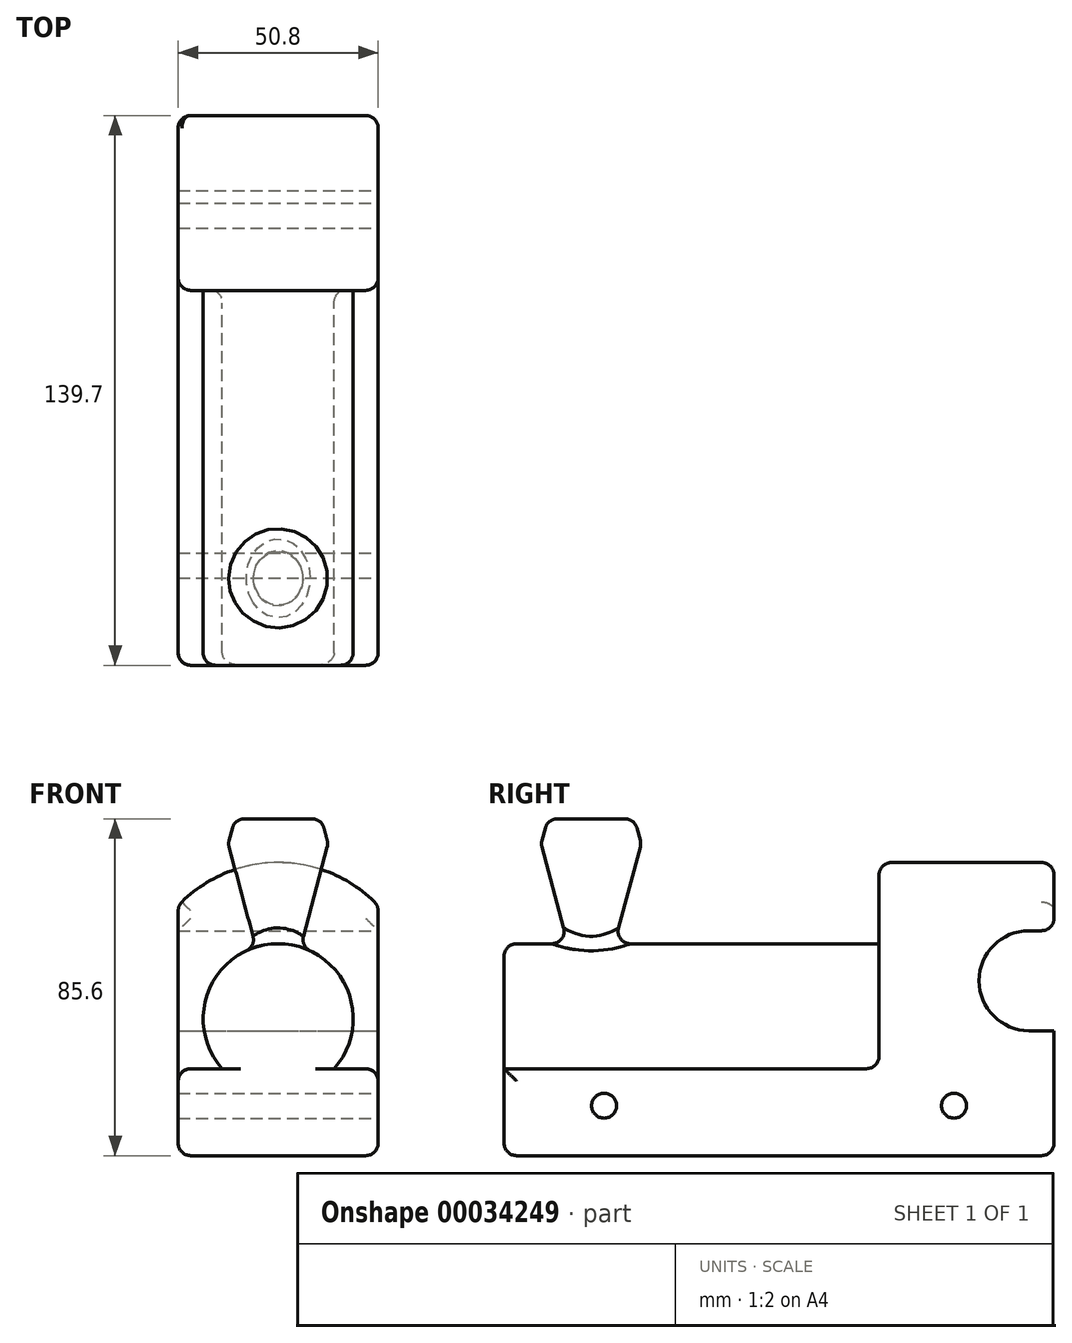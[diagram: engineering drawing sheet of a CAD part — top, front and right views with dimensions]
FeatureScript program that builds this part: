
annotation { "Feature Type Name" : "Feature", "Feature Type Description" : "" }
export const myFeature = defineFeature(function(context is Context, id is Id, definition is map)
    precondition{}
    {
        {
            var Q0;
            Q0=qCreatedBy(makeId("Front.planeOp"),FACE);
            var sketch = newSketch(context, id + "F0", { "sketchPlane" : qUnion([Q0])});
            skLineSegment(sketch, "E0.bottom", {"start": v(-39.2, 59.95) * mm, "end": v(11.6, 59.95) * mm});
            skLineSegment(sketch, "E0.top", {"start": v(-39.2, -3.55) * mm, "end": v(11.6, -3.55) * mm});
            skLineSegment(sketch, "E0.left", {"start": v(-39.2, 59.95) * mm, "end": v(-39.2, -3.55) * mm});
            skLineSegment(sketch, "E0.right", {"start": v(11.6, 59.95) * mm, "end": v(11.6, -3.55) * mm});
            skArc(sketch, "E1", {"start": v(11.6, 59.95) * mm, "mid": v(-13.8, 70.92) * mm, "end": v(-39.2, 59.95) * mm});
            skSolve(sketch);
        }
        {
            var Q0;
            Q0=makeQuery(id+"F0.imprint","IMPRINT",FACE,{"disambiguationData":[TD([[makeQuery(id+"F0.imprint","IMPRINT",EDGE,{"derivedFrom":sQuery(id+"F0.wireOp",EDGE,"E0.bottom")}),1.0]])]});
            var Q1;
            Q1=makeQuery(id+"F0.imprint","IMPRINT",FACE,{"disambiguationData":[TD([[makeQuery(id+"F0.imprint","IMPRINT",EDGE,{"derivedFrom":sQuery(id+"F0.wireOp",EDGE,"E0.bottom")}),-1.0]])]});
            extrude(context, id + "F1", {"entities" : qUnion([Q0, Q1]), "depth" : 139.7 * mm});
        }
        {
            var Q0;
            Q0=makeQuery(id+"F1.opExtrude","CAP_FACE",FACE,{"disambiguationData":[OSD([sQuery(id+"F0.wireOp",EDGE,"E0.top"),sQuery(id+"F0.wireOp",EDGE,"E0.left"),sQuery(id+"F0.wireOp",EDGE,"E0.right"),sQuery(id+"F0.wireOp",EDGE,"E1")])],"isStart":false});
            var sketch = newSketch(context, id + "F2", { "sketchPlane" : qUnion([Q0])});
            skLineSegment(sketch, "E2.bottom", {"start": v(-76.26, 116.12) * mm, "end": v(58.58, 116.12) * mm});
            skLineSegment(sketch, "E2.top", {"start": v(-76.26, 18.55) * mm, "end": v(58.58, 18.55) * mm});
            skLineSegment(sketch, "E2.left", {"start": v(-76.26, 116.12) * mm, "end": v(-76.26, 18.55) * mm});
            skLineSegment(sketch, "E2.right", {"start": v(58.58, 116.12) * mm, "end": v(58.58, 18.55) * mm});
            skSolve(sketch);
        }
        {
            var Q0;
            Q0=makeQuery(id+"F2.imprint","IMPRINT",FACE,{"disambiguationData":[TD([[makeQuery(id+"F2.imprint","IMPRINT",EDGE,{"derivedFrom":sQuery(id+"F2.wireOp",EDGE,"E2.bottom")}),-1.0]])]});
            var Q1;
            {var subQ3=makeQuery(id+"F1.opExtrude","CAP_EDGE",EDGE,{"disambiguationData":[OSD([sQuery(id+"F0.wireOp",EDGE,"E1")])],"isStart":false});Q1=makeQuery(id+"F2.imprint","IMPRINT",FACE,{"disambiguationData":[TD([[makeQuery(id+"F2.imprint","IMPRINT",EDGE,{"derivedFrom":subQ3}),1.0]])]});}
            extrude(context, id + "F3", {"entities" : qUnion([Q0, Q1]), "operationType" : NewBodyOperationType.REMOVE, "oppositeDirection" : true, "depth" : 95.25 * mm});
        }
        {
            var Q0;
            Q0=makeQuery(id+"F3.boolean.opBoolean","COPY",FACE,{"derivedFrom":makeQuery(id+"F3.opExtrude","CAP_FACE",FACE,{"disambiguationData":[OSD([sQuery(id+"F2.wireOp",EDGE,"E2.bottom"),sQuery(id+"F2.wireOp",EDGE,"E2.top"),sQuery(id+"F2.wireOp",EDGE,"E2.left"),sQuery(id+"F2.wireOp",EDGE,"E2.right")])],"isStart":false})});
            var sketch = newSketch(context, id + "F4", { "sketchPlane" : qUnion([Q0])});
            skCircle(sketch, "E3", {"center": v(-13.8, 31.25) * mm, "radius": 19.05 * mm});
            skPoint(sketch, "E4", {"position": v(-13.8, 50.3) * mm});
            skSolve(sketch);
        }
        {
            var Q0;
            {var subQ0=makeQuery(id+"F3.boolean.opBoolean","COPY",EDGE,{"derivedFrom":makeQuery(id+"F3.opExtrude","CAP_EDGE",EDGE,{"disambiguationData":[OSD([sQuery(id+"F2.wireOp",EDGE,"E2.top")])],"isStart":false})});var subQ1=sQuery(id+"F4.wireOp",EDGE,"E3");var subQ3=makeQuery(id+"F4.imprint","INTERSECT",VERTEX,{"disambiguationData":[OD(0.0)],"derivedFrom":[subQ0,subQ1]});Q0=makeQuery(id+"F4.imprint","IMPRINT",FACE,{"disambiguationData":[TD([[makeQuery(id+"F4.imprint","IMPRINT",EDGE,{"disambiguationData":[TD([[subQ3,1.0]])],"derivedFrom":subQ1}),1.0]])]});}
            extrude(context, id + "F5", {"entities" : qUnion([Q0]), "operationType" : NewBodyOperationType.ADD, "depth" : 95.25 * mm});
        }
        {
            var Q0;
            Q0=makeQuery(id+"F1.opExtrude","SWEPT_FACE",FACE,{"disambiguationData":[OSD([sQuery(id+"F0.wireOp",EDGE,"E0.right")])]});
            var sketch = newSketch(context, id + "F6", { "sketchPlane" : qUnion([Q0])});
            skLineSegment(sketch, "E5.bottom", {"start": v(-6.35, 53.6) * mm, "end": v(17.5, 53.6) * mm});
            skLineSegment(sketch, "E5.top", {"start": v(-6.35, 28.2) * mm, "end": v(17.5, 28.2) * mm});
            skLineSegment(sketch, "E5.left", {"start": v(-6.35, 53.6) * mm, "end": v(-6.35, 28.2) * mm});
            skLineSegment(sketch, "E5.right", {"start": v(17.5, 53.6) * mm, "end": v(17.5, 28.2) * mm});
            skArc(sketch, "E6", {"start": v(-6.35, 53.6) * mm, "mid": v(-19.05, 40.9) * mm, "end": v(-6.35, 28.2) * mm});
            skSolve(sketch);
        }
        {
            var Q0;
            Q0=makeQuery(id+"F6.imprint","IMPRINT",FACE,{"disambiguationData":[TD([[makeQuery(id+"F6.imprint","IMPRINT",EDGE,{"derivedFrom":sQuery(id+"F6.wireOp",EDGE,"E5.left")}),-1.0]])]});
            var Q1;
            {var subQ5=sQuery(id+"F6.wireOp",EDGE,"E5.left");Q1=makeQuery(id+"F6.imprint","IMPRINT",FACE,{"disambiguationData":[TD([[makeQuery(id+"F6.imprint","IMPRINT",EDGE,{"derivedFrom":subQ5}),1.0]])]});}
            extrude(context, id + "F7", {"entities" : qUnion([Q0, Q1]), "operationType" : NewBodyOperationType.REMOVE, "oppositeDirection" : true, "depth" : 50.8 * mm});
        }
        {
            var Q0;
            Q0=makeQuery(id+"F1.opExtrude","SWEPT_FACE",FACE,{"disambiguationData":[OSD([sQuery(id+"F0.wireOp",EDGE,"E0.right")])]});
            var sketch = newSketch(context, id + "F8", { "sketchPlane" : qUnion([Q0])});
            skPoint(sketch, "E7", {"position": v(-114.3, 9.15) * mm});
            skPoint(sketch, "E8", {"position": v(-25.4, 9.15) * mm});
            skSolve(sketch);
        }
        {
            var Q0;
            Q0=sQuery(id+"F8.wireOp",VERTEX,"E7");
            var Q1;
            Q1=sQuery(id+"F8.wireOp",VERTEX,"E8");
            var Q2;
            Q2=makeQuery(id+"F1.opExtrude","SWEPT_BODY",BODY,{"disambiguationData":[OSD([sQuery(id+"F0.wireOp",EDGE,"E0.top"),sQuery(id+"F0.wireOp",EDGE,"E0.left"),sQuery(id+"F0.wireOp",EDGE,"E0.right"),sQuery(id+"F0.wireOp",EDGE,"E1")])]});
            hole(context, id + "F9", {"style" : HoleStyle.SIMPLE, "holeDiameter" : 6.35 * mm, "endStyle" : HoleEndStyle.THROUGH, "locations" : qUnion([Q0, Q1]), "scope" : qUnion([Q2])});
        }
        {
            var Q0;
            Q0=sQuery(id+"F4.wireOp",VERTEX,"E4");
            var Q1;
            Q1=qCreatedBy(makeId("Top.planeOp"),FACE);
            cPlane(context, id + "F10", {"entities" : qUnion([Q0, Q1]), "cplaneType" : CPlaneType.PLANE_POINT, "offset" : 152.4 * mm, "width" : 152.4 * mm, "height" : 152.4 * mm});
        }
        {
            var Q0;
            Q0=qCreatedBy(id+"F10.planeOp",FACE);
            cPlane(context, id + "F11", {"entities" : qUnion([Q0]), "cplaneType" : CPlaneType.OFFSET, "offset" : 25.4 * mm, "width" : 152.4 * mm, "height" : 152.4 * mm});
        }
        {
            var Q0;
            Q0=qCreatedBy(id+"F11.planeOp",FACE);
            var sketch = newSketch(context, id + "F12", { "sketchPlane" : qUnion([Q0])});
            skCircle(sketch, "E9", {"center": v(-13.8, -117.6) * mm, "radius": 12.7 * mm});
            skSolve(sketch);
        }
        {
            var Q0;
            Q0=makeQuery(id+"F12.imprint","IMPRINT",FACE,{"disambiguationData":[TD([[makeQuery(id+"F12.imprint","IMPRINT",EDGE,{"derivedFrom":sQuery(id+"F12.wireOp",EDGE,"E9")}),1.0]])]});
            extrude(context, id + "F13", {"entities" : qUnion([Q0]), "operationType" : NewBodyOperationType.ADD, "oppositeDirection" : true, "depth" : 30.48 * mm, "hasDraft" : true, "draftAngle" : 15 * degree, "draftPullDirection" : true, "hasSecondDirection" : true, "secondDirectionOppositeDirection" : false, "secondDirectionDepth" : 6.35 * mm, "hasSecondDirectionDraft" : true, "secondDirectionDraftAngle" : 15 * degree, "secondDirectionDraftPullDirection" : true});
        }
        {
            var Q0;
            Q0=makeQuery(id+"F1.opExtrude","SWEPT_EDGE",EDGE,{"disambiguationData":[OSD([sQuery(id+"F0.wireOp",EDGE,"E0.bottom"),sQuery(id+"F0.wireOp",EDGE,"E0.left"),sQuery(id+"F0.wireOp",EDGE,"E1")])]});
            var Q1;
            Q1=makeQuery(id+"F7.boolean.opBoolean","COPY",EDGE,{"derivedFrom":makeQuery(id+"F7.opExtrude","SWEPT_EDGE",EDGE,{"disambiguationData":[OSD([sQuery(id+"F0.wireOp",EDGE,"E0.right"),sQuery(id+"F6.wireOp",EDGE,"E5.bottom")])]})});
            var Q2;
            Q2=makeQuery(id+"F7.boolean.opBoolean","COPY",EDGE,{"derivedFrom":makeQuery(id+"F7.opExtrude","CAP_EDGE",EDGE,{"disambiguationData":[OSD([sQuery(id+"F6.wireOp",EDGE,"E6")])],"isStart":true})});
            var Q3;
            Q3=makeQuery(id+"F7.boolean.opBoolean","COPY",EDGE,{"derivedFrom":makeQuery(id+"F7.opExtrude","CAP_EDGE",EDGE,{"disambiguationData":[OSD([sQuery(id+"F6.wireOp",EDGE,"E5.bottom")])],"isStart":true})});
            var Q4;
            Q4=makeQuery(id+"F7.boolean.opBoolean","COPY",EDGE,{"derivedFrom":makeQuery(id+"F7.opExtrude","CAP_EDGE",EDGE,{"disambiguationData":[OSD([sQuery(id+"F6.wireOp",EDGE,"E5.top")])],"isStart":true})});
            var Q5;
            Q5=makeQuery(id+"F7.boolean.opBoolean","COPY",EDGE,{"derivedFrom":makeQuery(id+"F7.opExtrude","SWEPT_EDGE",EDGE,{"disambiguationData":[OSD([sQuery(id+"F0.wireOp",EDGE,"E0.right"),sQuery(id+"F6.wireOp",EDGE,"E5.top")])]})});
            var Q6;
            Q6=makeQuery(id+"F7.boolean.opBoolean","COPY",EDGE,{"derivedFrom":makeQuery(id+"F7.opExtrude","CAP_EDGE",EDGE,{"disambiguationData":[OSD([sQuery(id+"F6.wireOp",EDGE,"E6")])],"isStart":false})});
            var Q7;
            Q7=makeQuery(id+"F7.boolean.opBoolean","COPY",EDGE,{"derivedFrom":makeQuery(id+"F7.opExtrude","CAP_EDGE",EDGE,{"disambiguationData":[OSD([sQuery(id+"F6.wireOp",EDGE,"E5.top")])],"isStart":false})});
            var Q8;
            Q8=makeQuery(id+"F7.boolean.opBoolean","COPY",EDGE,{"derivedFrom":makeQuery(id+"F7.opExtrude","CAP_EDGE",EDGE,{"disambiguationData":[OSD([sQuery(id+"F6.wireOp",EDGE,"E5.bottom")])],"isStart":false})});
            var Q9;
            Q9=makeQuery(id+"F1.opExtrude","CAP_EDGE",EDGE,{"disambiguationData":[OSD([sQuery(id+"F0.wireOp",EDGE,"E1")])],"isStart":true});
            var Q10;
            {var subQ0=sQuery(id+"F0.wireOp",EDGE,"E0.left");var subQ1=sQuery(id+"F0.wireOp",EDGE,"E1");Q10=makeQuery(id+"F7.boolean.opBoolean","SPLIT",EDGE,{"disambiguationData":[TD([makeQuery(id+"F1.opExtrude","SWEPT_FACE",FACE,{"disambiguationData":[OSD([subQ1])]})])],"derivedFrom":makeQuery(id+"F1.opExtrude","CAP_EDGE",EDGE,{"disambiguationData":[OSD([subQ0])],"isStart":true})});}
            var Q11;
            {var subQ0=sQuery(id+"F0.wireOp",EDGE,"E0.right");var subQ1=sQuery(id+"F0.wireOp",EDGE,"E1");Q11=makeQuery(id+"F7.boolean.opBoolean","SPLIT",EDGE,{"disambiguationData":[TD([makeQuery(id+"F1.opExtrude","SWEPT_FACE",FACE,{"disambiguationData":[OSD([subQ1])]})])],"derivedFrom":makeQuery(id+"F1.opExtrude","CAP_EDGE",EDGE,{"disambiguationData":[OSD([subQ0])],"isStart":true})});}
            var Q12;
            {var subQ0=sQuery(id+"F0.wireOp",EDGE,"E0.right");var subQ1=sQuery(id+"F0.wireOp",EDGE,"E0.top");Q12=makeQuery(id+"F7.boolean.opBoolean","SPLIT",EDGE,{"disambiguationData":[TD([makeQuery(id+"F1.opExtrude","SWEPT_FACE",FACE,{"disambiguationData":[OSD([subQ1])]})])],"derivedFrom":makeQuery(id+"F1.opExtrude","CAP_EDGE",EDGE,{"disambiguationData":[OSD([subQ0])],"isStart":true})});}
            var Q13;
            Q13=makeQuery(id+"F1.opExtrude","CAP_EDGE",EDGE,{"disambiguationData":[OSD([sQuery(id+"F0.wireOp",EDGE,"E0.top")])],"isStart":true});
            var Q14;
            {var subQ0=sQuery(id+"F0.wireOp",EDGE,"E0.left");var subQ1=sQuery(id+"F0.wireOp",EDGE,"E0.top");Q14=makeQuery(id+"F7.boolean.opBoolean","SPLIT",EDGE,{"disambiguationData":[TD([makeQuery(id+"F1.opExtrude","SWEPT_FACE",FACE,{"disambiguationData":[OSD([subQ1])]})])],"derivedFrom":makeQuery(id+"F1.opExtrude","CAP_EDGE",EDGE,{"disambiguationData":[OSD([subQ0])],"isStart":true})});}
            var Q15;
            Q15=makeQuery(id+"F1.opExtrude","SWEPT_EDGE",EDGE,{"disambiguationData":[OSD([sQuery(id+"F0.wireOp",EDGE,"E0.top"),sQuery(id+"F0.wireOp",EDGE,"E0.right")])]});
            var Q16;
            Q16=makeQuery(id+"F3.boolean.opBoolean","INTERSECT",EDGE,{"derivedFrom":[makeQuery(id+"F1.opExtrude","SWEPT_FACE",FACE,{"disambiguationData":[OSD([sQuery(id+"F0.wireOp",EDGE,"E0.right")])]}),makeQuery(id+"F3.opExtrude","SWEPT_FACE",FACE,{"disambiguationData":[OSD([sQuery(id+"F2.wireOp",EDGE,"E2.top")])]})]});
            var Q17;
            Q17=makeQuery(id+"F3.boolean.opBoolean","INTERSECT",EDGE,{"derivedFrom":[makeQuery(id+"F1.opExtrude","SWEPT_FACE",FACE,{"disambiguationData":[OSD([sQuery(id+"F0.wireOp",EDGE,"E0.right")])]}),makeQuery(id+"F3.opExtrude","CAP_FACE",FACE,{"disambiguationData":[OSD([sQuery(id+"F2.wireOp",EDGE,"E2.bottom"),sQuery(id+"F2.wireOp",EDGE,"E2.top"),sQuery(id+"F2.wireOp",EDGE,"E2.left"),sQuery(id+"F2.wireOp",EDGE,"E2.right")])],"isStart":false})]});
            var Q18;
            Q18=makeQuery(id+"F1.opExtrude","SWEPT_EDGE",EDGE,{"disambiguationData":[OSD([sQuery(id+"F0.wireOp",EDGE,"E0.bottom"),sQuery(id+"F0.wireOp",EDGE,"E0.right"),sQuery(id+"F0.wireOp",EDGE,"E1")])]});
            var Q19;
            Q19=makeQuery(id+"F3.boolean.opBoolean","INTERSECT",EDGE,{"derivedFrom":[makeQuery(id+"F1.opExtrude","SWEPT_FACE",FACE,{"disambiguationData":[OSD([sQuery(id+"F0.wireOp",EDGE,"E1")])]}),makeQuery(id+"F3.opExtrude","CAP_FACE",FACE,{"disambiguationData":[OSD([sQuery(id+"F2.wireOp",EDGE,"E2.bottom"),sQuery(id+"F2.wireOp",EDGE,"E2.top"),sQuery(id+"F2.wireOp",EDGE,"E2.left"),sQuery(id+"F2.wireOp",EDGE,"E2.right")])],"isStart":false})]});
            var Q20;
            Q20=makeQuery(id+"F3.boolean.opBoolean","INTERSECT",EDGE,{"derivedFrom":[makeQuery(id+"F1.opExtrude","SWEPT_FACE",FACE,{"disambiguationData":[OSD([sQuery(id+"F0.wireOp",EDGE,"E0.left")])]}),makeQuery(id+"F3.opExtrude","CAP_FACE",FACE,{"disambiguationData":[OSD([sQuery(id+"F2.wireOp",EDGE,"E2.bottom"),sQuery(id+"F2.wireOp",EDGE,"E2.top"),sQuery(id+"F2.wireOp",EDGE,"E2.left"),sQuery(id+"F2.wireOp",EDGE,"E2.right")])],"isStart":false})]});
            var Q21;
            Q21=makeQuery(id+"F3.boolean.opBoolean","INTERSECT",EDGE,{"derivedFrom":[makeQuery(id+"F1.opExtrude","SWEPT_FACE",FACE,{"disambiguationData":[OSD([sQuery(id+"F0.wireOp",EDGE,"E0.left")])]}),makeQuery(id+"F3.opExtrude","SWEPT_FACE",FACE,{"disambiguationData":[OSD([sQuery(id+"F2.wireOp",EDGE,"E2.top")])]})]});
            var Q22;
            Q22=makeQuery(id+"F1.opExtrude","SWEPT_EDGE",EDGE,{"disambiguationData":[OSD([sQuery(id+"F0.wireOp",EDGE,"E0.top"),sQuery(id+"F0.wireOp",EDGE,"E0.left")])]});
            var Q23;
            Q23=makeQuery(id+"F1.opExtrude","CAP_EDGE",EDGE,{"disambiguationData":[OSD([sQuery(id+"F0.wireOp",EDGE,"E0.left")])],"isStart":false});
            var Q24;
            Q24=makeQuery(id+"F5.opExtrude","CAP_EDGE",EDGE,{"disambiguationData":[OSD([sQuery(id+"F4.wireOp",EDGE,"E3")])],"isStart":false});
            var Q25;
            {var subQ0=sQuery(id+"F2.wireOp",EDGE,"E2.top");var subQ2=sQuery(id+"F0.wireOp",EDGE,"E0.left");Q25=makeQuery(id+"F5.boolean.opBoolean","SPLIT",EDGE,{"disambiguationData":[TD([makeQuery(id+"F1.opExtrude","SWEPT_FACE",FACE,{"disambiguationData":[OSD([subQ2])]})])],"derivedFrom":makeQuery(id+"F3.boolean.opBoolean","COPY",EDGE,{"derivedFrom":makeQuery(id+"F3.opExtrude","CAP_EDGE",EDGE,{"disambiguationData":[OSD([subQ0])],"isStart":true})})});}
            var Q26;
            {var subQ0=sQuery(id+"F2.wireOp",EDGE,"E2.top");var subQ2=sQuery(id+"F0.wireOp",EDGE,"E0.right");Q26=makeQuery(id+"F5.boolean.opBoolean","SPLIT",EDGE,{"disambiguationData":[TD([makeQuery(id+"F1.opExtrude","SWEPT_FACE",FACE,{"disambiguationData":[OSD([subQ2])]})])],"derivedFrom":makeQuery(id+"F3.boolean.opBoolean","COPY",EDGE,{"derivedFrom":makeQuery(id+"F3.opExtrude","CAP_EDGE",EDGE,{"disambiguationData":[OSD([subQ0])],"isStart":true})})});}
            var Q27;
            Q27=makeQuery(id+"F1.opExtrude","CAP_EDGE",EDGE,{"disambiguationData":[OSD([sQuery(id+"F0.wireOp",EDGE,"E0.right")])],"isStart":false});
            var Q28;
            Q28=makeQuery(id+"F1.opExtrude","CAP_EDGE",EDGE,{"disambiguationData":[OSD([sQuery(id+"F0.wireOp",EDGE,"E0.top")])],"isStart":false});
            var Q29;
            {var subQ0=sQuery(id+"F2.wireOp",EDGE,"E2.top");Q29=makeQuery(id+"F5.boolean.opBoolean","SPLIT",EDGE,{"disambiguationData":[TD([makeQuery(id+"F1.opExtrude","SWEPT_FACE",FACE,{"disambiguationData":[OSD([sQuery(id+"F0.wireOp",EDGE,"E0.right")])]})])],"derivedFrom":makeQuery(id+"F3.boolean.opBoolean","COPY",EDGE,{"derivedFrom":makeQuery(id+"F3.opExtrude","CAP_EDGE",EDGE,{"disambiguationData":[OSD([subQ0])],"isStart":false})})});}
            var Q30;
            {var subQ0=sQuery(id+"F2.wireOp",EDGE,"E2.top");Q30=makeQuery(id+"F5.boolean.opBoolean","SPLIT",EDGE,{"disambiguationData":[TD([makeQuery(id+"F1.opExtrude","SWEPT_FACE",FACE,{"disambiguationData":[OSD([sQuery(id+"F0.wireOp",EDGE,"E0.left")])]})])],"derivedFrom":makeQuery(id+"F3.boolean.opBoolean","COPY",EDGE,{"derivedFrom":makeQuery(id+"F3.opExtrude","CAP_EDGE",EDGE,{"disambiguationData":[OSD([subQ0])],"isStart":false})})});}
            var Q31;
            {var subQ0=makeQuery(id+"F13.opExtrude","SWEPT_FACE",FACE,{"disambiguationData":[OSD([sQuery(id+"F12.wireOp",EDGE,"E9")])]});Q31=makeQuery(id+"F13.*.booleanUnion.opBoolean","MERGE",EDGE,{"derivedFrom":[makeQuery(id+"F13.*.split.splitOp","SPLIT_SURFACE_INTERSECT",EDGE,{"derivedFrom":[subQ0]}),makeQuery(id+"F13.*.split.splitOp","SPLIT_SURFACE_INTERSECT",EDGE,{"derivedFrom":[subQ0],"isFromBackBody":true})]});}
            var Q32;
            Q32=makeQuery(id+"F13.opExtrude","CAP_EDGE",EDGE,{"disambiguationData":[OSD([sQuery(id+"F12.wireOp",EDGE,"E9")])],"isStart":true});
            var Q33;
            Q33=makeQuery(id+"F13.boolean.opBoolean","INTERSECT",EDGE,{"derivedFrom":[makeQuery(id+"F5.opExtrude","SWEPT_FACE",FACE,{"disambiguationData":[OSD([sQuery(id+"F4.wireOp",EDGE,"E3")])]}),makeQuery(id+"F13.*.split.splitOp","SPLIT",FACE,{"derivedFrom":makeQuery(id+"F13.opExtrude","SWEPT_FACE",FACE,{"disambiguationData":[OSD([sQuery(id+"F12.wireOp",EDGE,"E9")])]})})]});
            fillet(context, id + "F14", {"entities" : qUnion([Q0, Q1, Q2, Q3, Q4, Q5, Q6, Q7, Q8, Q9, Q10, Q11, Q12, Q13, Q14, Q15, Q16, Q17, Q18, Q19, Q20, Q21, Q22, Q23, Q24, Q25, Q26, Q27, Q28, Q29, Q30, Q31, Q32, Q33]), "radius" : 3.17 * mm, "tangentPropagation" : true, "allowEdgeOverflow" : false});
        }
    });
